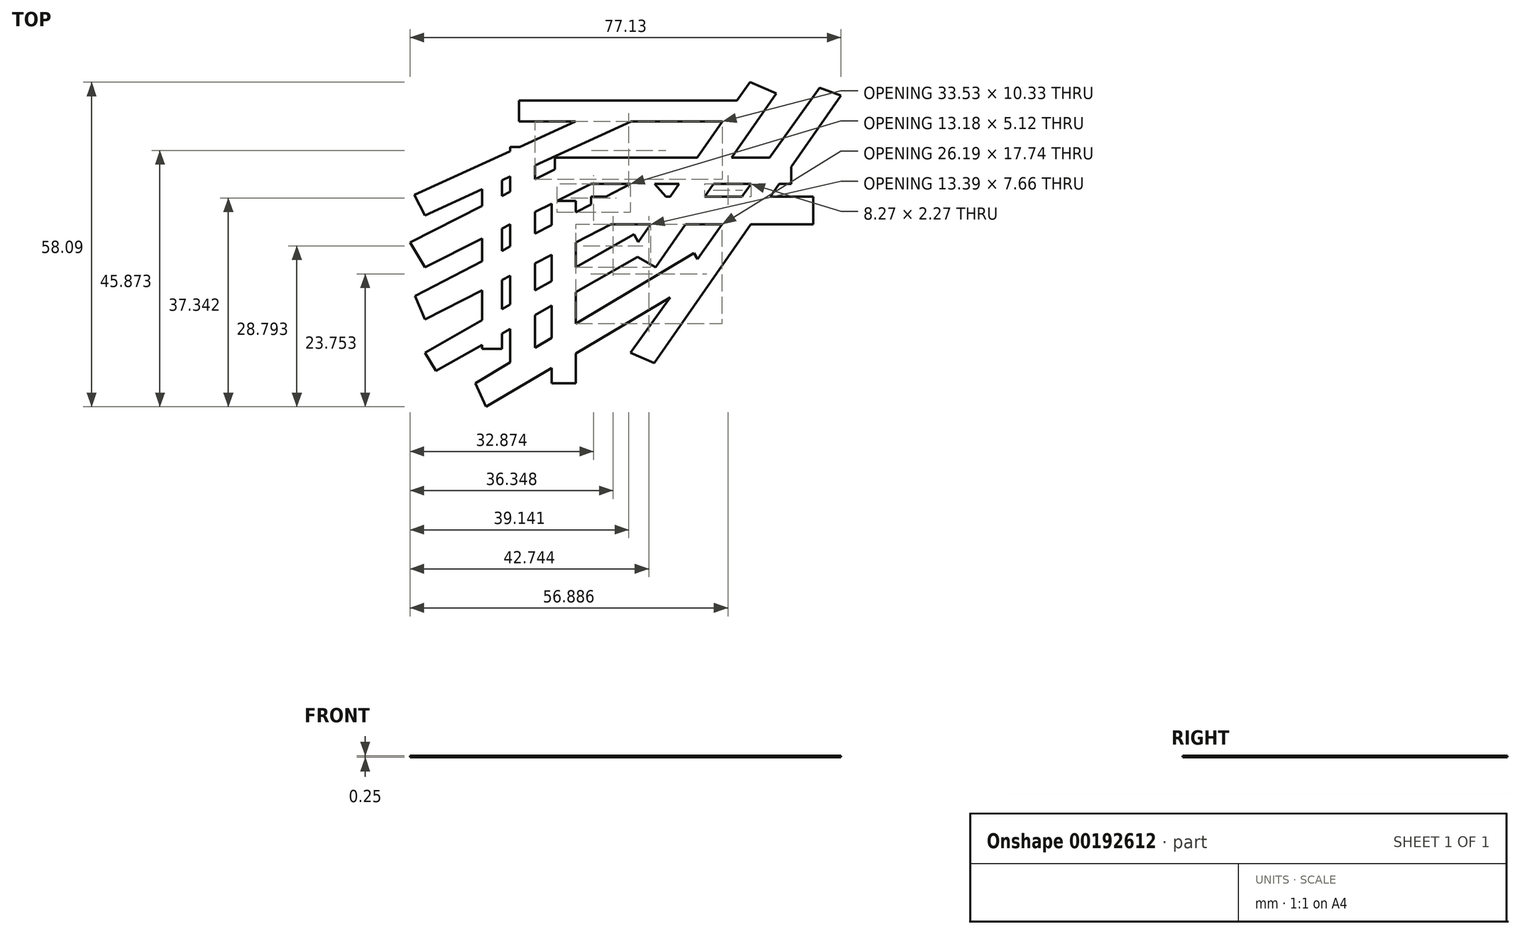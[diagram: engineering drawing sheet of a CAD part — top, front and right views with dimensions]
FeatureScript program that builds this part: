
annotation { "Feature Type Name" : "Feature", "Feature Type Description" : "" }
export const myFeature = defineFeature(function(context is Context, id is Id, definition is map)
    precondition{}
    {
        {
            var Q0;
            Q0=qCreatedBy(makeId("Top.planeOp"),FACE);
            var sketch = newSketch(context, id + "F0", { "sketchPlane" : qUnion([Q0])});
            skLineSegment(sketch, "E0.top", {"start": v(-18.06, -25) * mm, "end": v(-14.54, -25) * mm});
            skLineSegment(sketch, "E0.left", {"start": v(-18.06, 3.58) * mm, "end": v(-18.06, 0.6) * mm});
            skLineSegment(sketch, "E0.right", {"start": v(-14.54, 5.18) * mm, "end": v(-14.54, 2.38) * mm});
            skLineSegment(sketch, "E1.bottom", {"start": v(-11.47, 19.44) * mm, "end": v(27.53, 19.44) * mm});
            skLineSegment(sketch, "E1.top", {"start": v(-11.47, 15.69) * mm, "end": v(-1.37, 15.69) * mm});
            skLineSegment(sketch, "E1.left", {"start": v(-11.47, 19.44) * mm, "end": v(-11.47, 15.69) * mm});
            skLineSegment(sketch, "E2.bottom", {"start": v(-5.1, 9.21) * mm, "end": v(20.38, 9.21) * mm});
            skLineSegment(sketch, "E2.top", {"start": v(1.38, 4.55) * mm, "end": v(8.47, 4.55) * mm});
            skLineSegment(sketch, "E2.left", {"start": v(-5.1, 9.21) * mm, "end": v(-5.1, 7.13) * mm});
            skLineSegment(sketch, "E2.right", {"start": v(37.19, 7.56) * mm, "end": v(37.19, 4.55) * mm});
            skLineSegment(sketch, "E3.bottom", {"start": v(-13.06, 11.14) * mm, "end": v(-11.38, 11.14) * mm});
            skLineSegment(sketch, "E3.left", {"start": v(-13.06, 11.14) * mm, "end": v(-13.06, 10.38) * mm});
            skLineSegment(sketch, "E3.right", {"start": v(-8.62, 7.87) * mm, "end": v(-8.62, 5.36) * mm});
            skLineSegment(sketch, "E4.bottom", {"start": v(-4.72, 1.48) * mm, "end": v(-1.35, 1.48) * mm});
            skLineSegment(sketch, "E4.top", {"start": v(-5.67, -31.15) * mm, "end": v(-1.35, -31.15) * mm});
            skLineSegment(sketch, "E4.left", {"start": v(-5.67, 1) * mm, "end": v(-5.67, -2.82) * mm});
            skLineSegment(sketch, "E4.right", {"start": v(-1.35, 1.48) * mm, "end": v(-1.35, -0.57) * mm});
            skLineSegment(sketch, "E5.bottom", {"start": v(1.38, 2.28) * mm, "end": v(4.1, 2.28) * mm});
            skLineSegment(sketch, "E5.top", {"start": v(4.98, -2.73) * mm, "end": v(12.04, -2.73) * mm});
            skLineSegment(sketch, "E5.left", {"start": v(1.38, 2.28) * mm, "end": v(1.38, 0.86) * mm});
            skLineSegment(sketch, "E5.right", {"start": v(41.17, 2.28) * mm, "end": v(41.17, -2.73) * mm});
            skLineSegment(sketch, "E6", {"start": v(-17.38, -35.35) * mm, "end": v(-5.67, -28.39) * mm});
            skLineSegment(sketch, "E7", {"start": v(20.44, -8.9) * mm, "end": v(19.83, -7.87) * mm});
            skLineSegment(sketch, "E8", {"start": v(19.83, -7.87) * mm, "end": v(-1.35, -20.47) * mm});
            skLineSegment(sketch, "E9", {"start": v(-19.3, -31.15) * mm, "end": v(-17.38, -35.35) * mm});
            skLineSegment(sketch, "E10", {"start": v(-28.34, -25.69) * mm, "end": v(-26.31, -28.93) * mm});
            skLineSegment(sketch, "E11", {"start": v(-26.31, -28.93) * mm, "end": v(-18.06, -24.27) * mm});
            skLineSegment(sketch, "E12", {"start": v(9.87, -5.84) * mm, "end": v(9.1, -4.47) * mm});
            skLineSegment(sketch, "E13", {"start": v(9.1, -4.47) * mm, "end": v(-1.35, -10.39) * mm});
            skLineSegment(sketch, "E14", {"start": v(-28.34, -19.74) * mm, "end": v(-18.06, -14.5) * mm});
            skLineSegment(sketch, "E15", {"start": v(14.78, 2.28) * mm, "end": v(12.76, 4.55) * mm});
            skLineSegment(sketch, "E16", {"start": v(8.47, 4.55) * mm, "end": v(4.1, 2.28) * mm});
            skLineSegment(sketch, "E17", {"start": v(-30.1, -15.55) * mm, "end": v(-28.34, -19.74) * mm});
            skLineSegment(sketch, "E18", {"start": v(-28.34, -10.41) * mm, "end": v(-18.06, -5.24) * mm});
            skLineSegment(sketch, "E19", {"start": v(-5.1, 7.13) * mm, "end": v(-8.62, 5.36) * mm});
            skLineSegment(sketch, "E20", {"start": v(-31, -5.9) * mm, "end": v(-28.34, -10.41) * mm});
            skLineSegment(sketch, "E21", {"start": v(-28.34, -1.08) * mm, "end": v(-18.06, 3.58) * mm});
            skLineSegment(sketch, "E22", {"start": v(-1.37, 15.69) * mm, "end": v(-11.38, 11.14) * mm});
            skLineSegment(sketch, "E23", {"start": v(-30.24, 2.58) * mm, "end": v(-28.34, -1.08) * mm});
            skLineSegment(sketch, "E24", {"start": v(9.72, -8.56) * mm, "end": v(12.93, -10.41) * mm});
            skLineSegment(sketch, "E25", {"start": v(12.93, -10.41) * mm, "end": v(18.27, -2.73) * mm});
            skLineSegment(sketch, "E26", {"start": v(34.56, 20.71) * mm, "end": v(29.83, 22.74) * mm});
            skLineSegment(sketch, "E27", {"start": v(29.83, 22.74) * mm, "end": v(27.53, 19.44) * mm});
            skLineSegment(sketch, "E28", {"start": v(42.27, 21.73) * mm, "end": v(33.35, 9.21) * mm});
            skPoint(sketch, "E28.startSnap0", {"position": v(32.2, 21.73) * mm});
            skLineSegment(sketch, "E29", {"start": v(8.47, -25.69) * mm, "end": v(12.7, -27.5) * mm});
            skLineSegment(sketch, "E30", {"start": v(12.7, -27.5) * mm, "end": v(30, -2.73) * mm});
            skLineSegment(sketch, "E31", {"start": v(46.13, 20.36) * mm, "end": v(42.27, 21.73) * mm});
            skLineSegment(sketch, "E32.trimOffspring", {"start": v(-18.06, -14.5) * mm, "end": v(-18.06, -19.86) * mm});
            skLineSegment(sketch, "E33.trimOffspring", {"start": v(-18.06, -5.24) * mm, "end": v(-18.06, -9.27) * mm});
            skLineSegment(sketch, "E34.trimOffspring", {"start": v(-14.54, -3.46) * mm, "end": v(-14.54, -7.44) * mm});
            skLineSegment(sketch, "E35.trimOffspring", {"start": v(-13.06, -2.72) * mm, "end": v(-13.06, -6.67) * mm});
            skLineSegment(sketch, "E36.trimOffspring", {"start": v(-13.06, 5.86) * mm, "end": v(-13.06, 3.12) * mm});
            skLineSegment(sketch, "E37.trimOffspring", {"start": v(-8.62, -0.49) * mm, "end": v(-8.62, -4.36) * mm});
            skPoint(sketch, "E38.orphan", {"position": v(-5.1, 4.55) * mm});
            skLineSegment(sketch, "E39.trimOffspring", {"start": v(-14.54, -12.7) * mm, "end": v(-14.54, -17.86) * mm});
            skLineSegment(sketch, "E40.trimOffspring", {"start": v(-13.06, -11.94) * mm, "end": v(-13.06, -17.03) * mm});
            skLineSegment(sketch, "E41.trimOffspring", {"start": v(-8.62, -9.67) * mm, "end": v(-8.62, -14.51) * mm});
            skLineSegment(sketch, "E42.trimOffspring", {"start": v(-5.67, -8.16) * mm, "end": v(-5.67, -12.84) * mm});
            skLineSegment(sketch, "E43.trimOffspring", {"start": v(-1.35, -5.96) * mm, "end": v(-1.35, -10.39) * mm});
            skPoint(sketch, "E44.orphan", {"position": v(1.38, -2.73) * mm});
            skLineSegment(sketch, "E45.trimOffspring", {"start": v(14.78, 2.28) * mm, "end": v(15.54, 2.28) * mm});
            skLineSegment(sketch, "E46.trimOffspring", {"start": v(24.9, 15.69) * mm, "end": v(20.38, 9.21) * mm});
            skPoint(sketch, "E47.orphan", {"position": v(28.66, 15.69) * mm});
            skLineSegment(sketch, "E48.trimOffspring", {"start": v(35.08, 4.55) * mm, "end": v(37.19, 4.55) * mm});
            skLineSegment(sketch, "E49.trimOffspring", {"start": v(33.5, 2.28) * mm, "end": v(41.17, 2.28) * mm});
            skLineSegment(sketch, "E50.trimOffspring", {"start": v(30, -2.73) * mm, "end": v(41.17, -2.73) * mm});
            skLineSegment(sketch, "E51.trimOffspring", {"start": v(23.33, 4.55) * mm, "end": v(30.02, 4.55) * mm});
            skLineSegment(sketch, "E52.trimOffspring", {"start": v(26.57, 9.21) * mm, "end": v(33.35, 9.21) * mm});
            skLineSegment(sketch, "E53.trimOffspring", {"start": v(26.57, 9.21) * mm, "end": v(34.56, 20.71) * mm});
            skLineSegment(sketch, "E54.trimOffspring", {"start": v(17.13, 4.55) * mm, "end": v(15.54, 2.28) * mm});
            skLineSegment(sketch, "E55.trimOffspring", {"start": v(21.75, 2.28) * mm, "end": v(28.4, 2.28) * mm});
            skLineSegment(sketch, "E56.trimOffspring", {"start": v(18.27, -2.73) * mm, "end": v(24.84, -2.73) * mm});
            skPoint(sketch, "E57.orphan", {"position": v(8.47, -7.84) * mm});
            skPoint(sketch, "E58.orphan", {"position": v(11, -7.84) * mm});
            skLineSegment(sketch, "E59.trimOffspring", {"start": v(1.38, 0.86) * mm, "end": v(-1.35, -0.57) * mm});
            skLineSegment(sketch, "E60.trimOffspring", {"start": v(12.04, -2.73) * mm, "end": v(9.87, -5.84) * mm});
            skLineSegment(sketch, "E61.trimOffspring", {"start": v(21.75, 2.28) * mm, "end": v(23.33, 4.55) * mm});
            skLineSegment(sketch, "E62.trimOffspring", {"start": v(24.84, -2.73) * mm, "end": v(20.44, -8.9) * mm});
            skLineSegment(sketch, "E63.trimOffspring", {"start": v(33.5, 2.28) * mm, "end": v(35.08, 4.55) * mm});
            skLineSegment(sketch, "E64.trimOffspring", {"start": v(30.02, 4.55) * mm, "end": v(28.4, 2.28) * mm});
            skLineSegment(sketch, "E65.trimOffspring", {"start": v(37.19, 7.56) * mm, "end": v(46.13, 20.36) * mm});
            skLineSegment(sketch, "E66.trimOffspring", {"start": v(-14.54, 5.18) * mm, "end": v(-13.06, 5.86) * mm});
            skLineSegment(sketch, "E67.trimOffspring", {"start": v(-8.62, 7.87) * mm, "end": v(8.6, 15.69) * mm});
            skLineSegment(sketch, "E68.trimOffspring", {"start": v(-13.06, 3.12) * mm, "end": v(-14.54, 2.38) * mm});
            skLineSegment(sketch, "E69.trimOffspring", {"start": v(-18.06, 0.6) * mm, "end": v(-31, -5.9) * mm});
            skLineSegment(sketch, "E70.trimOffspring", {"start": v(12.76, 4.55) * mm, "end": v(17.13, 4.55) * mm});
            skLineSegment(sketch, "E71.trimOffspring", {"start": v(-5.67, -2.82) * mm, "end": v(-8.62, -4.36) * mm});
            skLineSegment(sketch, "E72.trimOffspring", {"start": v(-1.35, -5.96) * mm, "end": v(4.98, -2.73) * mm});
            skLineSegment(sketch, "E73.trimOffspring", {"start": v(-13.06, -6.67) * mm, "end": v(-14.54, -7.44) * mm});
            skLineSegment(sketch, "E74.trimOffspring", {"start": v(-18.06, -9.27) * mm, "end": v(-30.1, -15.55) * mm});
            skLineSegment(sketch, "E75.trimOffspring", {"start": v(-14.54, -12.7) * mm, "end": v(-13.06, -11.94) * mm});
            skLineSegment(sketch, "E76.trimOffspring", {"start": v(-8.62, -9.67) * mm, "end": v(-5.67, -8.16) * mm});
            skLineSegment(sketch, "E77.trimOffspring", {"start": v(-14.54, -22.28) * mm, "end": v(-14.54, -25) * mm});
            skLineSegment(sketch, "E78.trimOffspring", {"start": v(-18.06, -24.27) * mm, "end": v(-18.06, -25) * mm});
            skLineSegment(sketch, "E79.trimOffspring", {"start": v(-14.54, -22.28) * mm, "end": v(-13.06, -21.44) * mm});
            skLineSegment(sketch, "E80.trimOffspring", {"start": v(-18.06, -19.86) * mm, "end": v(-28.34, -25.69) * mm});
            skLineSegment(sketch, "E81.trimOffspring", {"start": v(-14.54, -3.46) * mm, "end": v(-13.06, -2.72) * mm});
            skLineSegment(sketch, "E82.trimOffspring", {"start": v(-8.62, -0.49) * mm, "end": v(-5.67, 1) * mm});
            skLineSegment(sketch, "E83.trimOffspring", {"start": v(-13.06, -17.03) * mm, "end": v(-14.54, -17.86) * mm});
            skLineSegment(sketch, "E84.trimOffspring", {"start": v(-8.62, -18.93) * mm, "end": v(-5.67, -17.26) * mm});
            skLineSegment(sketch, "E85.trimOffspring", {"start": v(-5.67, -12.84) * mm, "end": v(-8.62, -14.51) * mm});
            skLineSegment(sketch, "E86.trimOffspring", {"start": v(-1.35, -14.82) * mm, "end": v(9.72, -8.56) * mm});
            skLineSegment(sketch, "E87.trimOffspring", {"start": v(-5.67, -17.26) * mm, "end": v(-5.67, -23.04) * mm});
            skLineSegment(sketch, "E88.trimOffspring", {"start": v(-1.35, -14.82) * mm, "end": v(-1.35, -20.47) * mm});
            skLineSegment(sketch, "E89.trimOffspring", {"start": v(-8.62, -18.93) * mm, "end": v(-8.62, -24.8) * mm});
            skLineSegment(sketch, "E90.trimOffspring", {"start": v(-13.06, -21.44) * mm, "end": v(-13.06, -27.43) * mm});
            skLineSegment(sketch, "E91.trimOffspring", {"start": v(-13.06, -27.43) * mm, "end": v(-19.3, -31.15) * mm});
            skLineSegment(sketch, "E92.trimOffspring", {"start": v(-5.67, -28.39) * mm, "end": v(-5.67, -31.15) * mm});
            skLineSegment(sketch, "E93.trimOffspring", {"start": v(-1.35, -25.82) * mm, "end": v(-1.35, -31.15) * mm});
            skLineSegment(sketch, "E94.trimOffspring", {"start": v(-5.67, -23.04) * mm, "end": v(-8.62, -24.8) * mm});
            skLineSegment(sketch, "E95.trimOffspring", {"start": v(-1.35, -25.82) * mm, "end": v(15.54, -15.77) * mm});
            skLineSegment(sketch, "E96.trimOffspring", {"start": v(15.54, -15.77) * mm, "end": v(8.47, -25.69) * mm});
            skLineSegment(sketch, "E97.trimOffspring", {"start": v(-4.72, 1.48) * mm, "end": v(1.38, 4.55) * mm});
            skLineSegment(sketch, "E98.trimOffspring", {"start": v(-13.06, 10.38) * mm, "end": v(-30.24, 2.58) * mm});
            skLineSegment(sketch, "E99.trimOffspring", {"start": v(8.6, 15.69) * mm, "end": v(24.9, 15.69) * mm});
            skSolve(sketch);
        }
        {
            var Q0;
            Q0 = qSketchRegion(id + "F0", true);
            extrude(context, id + "F1", {"entities" : qUnion([Q0]), "depth" : .25 * mm});
        }
    });
